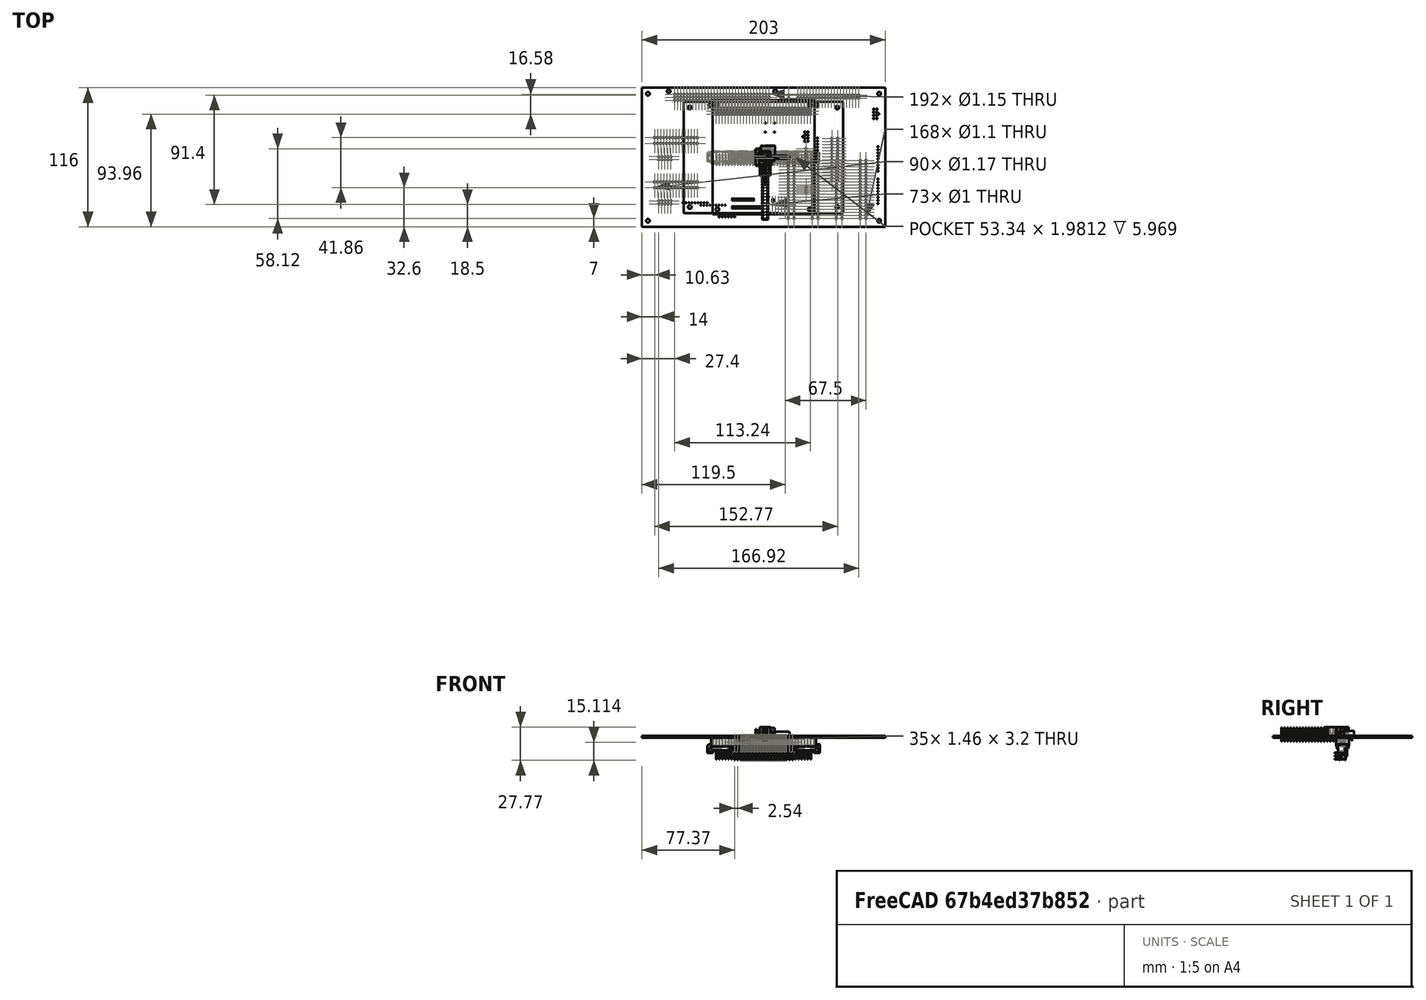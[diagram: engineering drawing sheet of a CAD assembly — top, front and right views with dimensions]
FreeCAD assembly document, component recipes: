
FREECAD ASSEMBLY — COMPONENT RECIPES ("GComputerCaseAssembly")

This assembly document has 216 components, labeled P0..P215 below (a component is one placed body or linked part). 0 of them carry a construction recipe — the FreeCAD feature program that regenerates the part from scratch, quoted from this document or its linked companion documents; the rest are supplied as boundary geometry only. No exploded tour is included for this assembly.
COMPONENT P0 — geometry summary ("FirstPartPeripherals"; no construction recipe available for this part):
  bounding box: 145.0 x 132.5 x 56.0 mm
  tessellated surface: 13,564 triangles
  volume: 118816 mm^3 (11% of its bounding box)
COMPONENT P1 — geometry summary ("SecondPartPeripherals"; no construction recipe available for this part):
  bounding box: 131.0 x 78.0 x 56.0 mm
  tessellated surface: 13,790 triangles
  volume: 66979 mm^3 (12% of its bounding box)
COMPONENT P2 — geometry summary ("FirstPartProcessor"; no construction recipe available for this part):
  bounding box: 147.0 x 120.6 x 56.0 mm
  tessellated surface: 38,998 triangles
  volume: 110022 mm^3 (11% of its bounding box)
COMPONENT P3 — geometry summary ("SecondPartProcessor"; no construction recipe available for this part):
  bounding box: 120.6 x 78.0 x 56.0 mm
  tessellated surface: 14,104 triangles
  volume: 61111 mm^3 (12% of its bounding box)
COMPONENT P4 — geometry summary ("C_0805_2012Metric001"; no construction recipe available for this part):
  bounding box: 2.0 x 1.2 x 1.2 mm
  tessellated surface: 188 triangles
  volume: 3 mm^3 (92% of its bounding box)
  symmetry: 4-fold rotationally symmetric about the x axis; 2-fold rotationally symmetric about the z axis; mirror-symmetric across its x mid-plane, y mid-plane
COMPONENT P5 — geometry summary ("C_0805_2012Metric002"; no construction recipe available for this part):
  bounding box: 2.0 x 1.2 x 1.2 mm
  tessellated surface: 188 triangles
  volume: 3 mm^3 (92% of its bounding box)
  symmetry: 4-fold rotationally symmetric about the x axis; 2-fold rotationally symmetric about the z axis; mirror-symmetric across its x mid-plane, y mid-plane
COMPONENT P6 — geometry summary ("C_0805_2012Metric003"; no construction recipe available for this part):
  bounding box: 2.0 x 1.2 x 1.2 mm
  tessellated surface: 188 triangles
  volume: 3 mm^3 (92% of its bounding box)
  symmetry: 4-fold rotationally symmetric about the x axis; 2-fold rotationally symmetric about the z axis; mirror-symmetric across its x mid-plane, y mid-plane
COMPONENT P7 — geometry summary ("C_0805_2012Metric004"; no construction recipe available for this part):
  bounding box: 2.0 x 1.2 x 1.2 mm
  tessellated surface: 188 triangles
  volume: 3 mm^3 (92% of its bounding box)
  symmetry: 4-fold rotationally symmetric about the x axis; 2-fold rotationally symmetric about the z axis; mirror-symmetric across its x mid-plane, y mid-plane
COMPONENT P8 — geometry summary ("C_0805_2012Metric005"; no construction recipe available for this part):
  bounding box: 2.0 x 1.2 x 1.2 mm
  tessellated surface: 188 triangles
  volume: 3 mm^3 (92% of its bounding box)
  symmetry: 4-fold rotationally symmetric about the x axis; 2-fold rotationally symmetric about the z axis; mirror-symmetric across its x mid-plane, y mid-plane
COMPONENT P9 — geometry summary ("C_0805_2012Metric006"; no construction recipe available for this part):
  bounding box: 2.0 x 1.2 x 1.2 mm
  tessellated surface: 188 triangles
  volume: 3 mm^3 (92% of its bounding box)
  symmetry: 4-fold rotationally symmetric about the x axis; 2-fold rotationally symmetric about the z axis; mirror-symmetric across its x mid-plane, y mid-plane
COMPONENT P10 — geometry summary ("C_0805_2012Metric007"; no construction recipe available for this part):
  bounding box: 2.0 x 1.2 x 1.2 mm
  tessellated surface: 188 triangles
  volume: 3 mm^3 (92% of its bounding box)
  symmetry: 4-fold rotationally symmetric about the x axis; 2-fold rotationally symmetric about the z axis; mirror-symmetric across its x mid-plane, y mid-plane
COMPONENT P11 — geometry summary ("C_0805_2012Metric008"; no construction recipe available for this part):
  bounding box: 2.0 x 1.2 x 1.2 mm
  tessellated surface: 188 triangles
  volume: 3 mm^3 (92% of its bounding box)
  symmetry: 4-fold rotationally symmetric about the x axis; 2-fold rotationally symmetric about the z axis; mirror-symmetric across its x mid-plane, y mid-plane
COMPONENT P12 — geometry summary ("C_0805_2012Metric009"; no construction recipe available for this part):
  bounding box: 2.0 x 1.2 x 1.2 mm
  tessellated surface: 188 triangles
  volume: 3 mm^3 (92% of its bounding box)
  symmetry: 4-fold rotationally symmetric about the x axis; 2-fold rotationally symmetric about the z axis; mirror-symmetric across its x mid-plane, y mid-plane
COMPONENT P13 — geometry summary ("C_0805_2012Metric010"; no construction recipe available for this part):
  bounding box: 2.0 x 1.2 x 1.2 mm
  tessellated surface: 188 triangles
  volume: 3 mm^3 (92% of its bounding box)
  symmetry: 4-fold rotationally symmetric about the x axis; 2-fold rotationally symmetric about the z axis; mirror-symmetric across its x mid-plane, y mid-plane
COMPONENT P14 — geometry summary ("C_0805_2012Metric011"; no construction recipe available for this part):
  bounding box: 2.0 x 1.2 x 1.2 mm
  tessellated surface: 188 triangles
  volume: 3 mm^3 (92% of its bounding box)
  symmetry: 4-fold rotationally symmetric about the x axis; 2-fold rotationally symmetric about the z axis; mirror-symmetric across its x mid-plane, y mid-plane
COMPONENT P15 — geometry summary ("C_0805_2012Metric012"; no construction recipe available for this part):
  bounding box: 2.0 x 1.2 x 1.2 mm
  tessellated surface: 188 triangles
  volume: 3 mm^3 (92% of its bounding box)
  symmetry: 4-fold rotationally symmetric about the x axis; 2-fold rotationally symmetric about the z axis; mirror-symmetric across its x mid-plane, y mid-plane
COMPONENT P16 — geometry summary ("C_0805_2012Metric013"; no construction recipe available for this part):
  bounding box: 2.0 x 1.2 x 1.2 mm
  tessellated surface: 188 triangles
  volume: 3 mm^3 (92% of its bounding box)
  symmetry: 4-fold rotationally symmetric about the x axis; 2-fold rotationally symmetric about the z axis; mirror-symmetric across its x mid-plane, y mid-plane
COMPONENT P17 — geometry summary ("C_0805_2012Metric014"; no construction recipe available for this part):
  bounding box: 2.0 x 1.2 x 1.2 mm
  tessellated surface: 188 triangles
  volume: 3 mm^3 (92% of its bounding box)
  symmetry: 4-fold rotationally symmetric about the x axis; 2-fold rotationally symmetric about the z axis; mirror-symmetric across its x mid-plane, y mid-plane
COMPONENT P18 — geometry summary ("C_0805_2012Metric015"; no construction recipe available for this part):
  bounding box: 2.0 x 1.2 x 1.2 mm
  tessellated surface: 188 triangles
  volume: 3 mm^3 (92% of its bounding box)
  symmetry: 4-fold rotationally symmetric about the x axis; 2-fold rotationally symmetric about the z axis; mirror-symmetric across its x mid-plane, y mid-plane
COMPONENT P19 — geometry summary ("C_0805_2012Metric016"; no construction recipe available for this part):
  bounding box: 2.0 x 1.2 x 1.2 mm
  tessellated surface: 188 triangles
  volume: 3 mm^3 (92% of its bounding box)
  symmetry: 4-fold rotationally symmetric about the x axis; 2-fold rotationally symmetric about the z axis; mirror-symmetric across its x mid-plane, y mid-plane
COMPONENT P20 — geometry summary ("C_0805_2012Metric017"; no construction recipe available for this part):
  bounding box: 2.0 x 1.2 x 1.2 mm
  tessellated surface: 188 triangles
  volume: 3 mm^3 (92% of its bounding box)
  symmetry: 4-fold rotationally symmetric about the x axis; 2-fold rotationally symmetric about the z axis; mirror-symmetric across its x mid-plane, y mid-plane
COMPONENT P21 — geometry summary ("C_0805_2012Metric018"; no construction recipe available for this part):
  bounding box: 2.0 x 1.2 x 1.2 mm
  tessellated surface: 188 triangles
  volume: 3 mm^3 (92% of its bounding box)
  symmetry: 4-fold rotationally symmetric about the x axis; 2-fold rotationally symmetric about the z axis; mirror-symmetric across its x mid-plane, y mid-plane
COMPONENT P22 — geometry summary ("C_0805_2012Metric019"; no construction recipe available for this part):
  bounding box: 2.0 x 1.2 x 1.2 mm
  tessellated surface: 188 triangles
  volume: 3 mm^3 (92% of its bounding box)
  symmetry: 4-fold rotationally symmetric about the x axis; 2-fold rotationally symmetric about the z axis; mirror-symmetric across its x mid-plane, y mid-plane
COMPONENT P23 — geometry summary ("C_0805_2012Metric020"; no construction recipe available for this part):
  bounding box: 2.0 x 1.2 x 1.2 mm
  tessellated surface: 188 triangles
  volume: 3 mm^3 (92% of its bounding box)
  symmetry: 4-fold rotationally symmetric about the x axis; 2-fold rotationally symmetric about the z axis; mirror-symmetric across its x mid-plane, y mid-plane
COMPONENT P24 — geometry summary ("C_0805_2012Metric021"; no construction recipe available for this part):
  bounding box: 2.0 x 1.2 x 1.2 mm
  tessellated surface: 188 triangles
  volume: 3 mm^3 (92% of its bounding box)
  symmetry: 4-fold rotationally symmetric about the x axis; 2-fold rotationally symmetric about the z axis; mirror-symmetric across its x mid-plane, y mid-plane
COMPONENT P25 — geometry summary ("C_0805_2012Metric022"; no construction recipe available for this part):
  bounding box: 2.0 x 1.2 x 1.2 mm
  tessellated surface: 188 triangles
  volume: 3 mm^3 (92% of its bounding box)
  symmetry: 4-fold rotationally symmetric about the x axis; 2-fold rotationally symmetric about the z axis; mirror-symmetric across its x mid-plane, y mid-plane
COMPONENT P26 — geometry summary ("C_0805_2012Metric023"; no construction recipe available for this part):
  bounding box: 2.0 x 1.2 x 1.2 mm
  tessellated surface: 188 triangles
  volume: 3 mm^3 (92% of its bounding box)
  symmetry: 4-fold rotationally symmetric about the x axis; 2-fold rotationally symmetric about the z axis; mirror-symmetric across its x mid-plane, y mid-plane
COMPONENT P27 — geometry summary ("C_0805_2012Metric024"; no construction recipe available for this part):
  bounding box: 2.0 x 1.2 x 1.2 mm
  tessellated surface: 188 triangles
  volume: 3 mm^3 (92% of its bounding box)
  symmetry: 4-fold rotationally symmetric about the x axis; 2-fold rotationally symmetric about the z axis; mirror-symmetric across its x mid-plane, y mid-plane
COMPONENT P28 — geometry summary ("C_0805_2012Metric025"; no construction recipe available for this part):
  bounding box: 2.0 x 1.2 x 1.2 mm
  tessellated surface: 188 triangles
  volume: 3 mm^3 (92% of its bounding box)
  symmetry: 4-fold rotationally symmetric about the x axis; 2-fold rotationally symmetric about the z axis; mirror-symmetric across its x mid-plane, y mid-plane
COMPONENT P29 — geometry summary ("C_0805_2012Metric026"; no construction recipe available for this part):
  bounding box: 2.0 x 1.2 x 1.2 mm
  tessellated surface: 188 triangles
  volume: 3 mm^3 (92% of its bounding box)
  symmetry: 4-fold rotationally symmetric about the x axis; 2-fold rotationally symmetric about the z axis; mirror-symmetric across its x mid-plane, y mid-plane
COMPONENT P30 — geometry summary ("C_0805_2012Metric027"; no construction recipe available for this part):
  bounding box: 2.0 x 1.2 x 1.2 mm
  tessellated surface: 188 triangles
  volume: 3 mm^3 (92% of its bounding box)
  symmetry: 4-fold rotationally symmetric about the x axis; 2-fold rotationally symmetric about the z axis; mirror-symmetric across its x mid-plane, y mid-plane
COMPONENT P31 — geometry summary ("C_0805_2012Metric028"; no construction recipe available for this part):
  bounding box: 2.0 x 1.2 x 1.2 mm
  tessellated surface: 188 triangles
  volume: 3 mm^3 (92% of its bounding box)
  symmetry: 4-fold rotationally symmetric about the x axis; 2-fold rotationally symmetric about the z axis; mirror-symmetric across its x mid-plane, y mid-plane
COMPONENT P32 — geometry summary ("C_0805_2012Metric029"; no construction recipe available for this part):
  bounding box: 2.0 x 1.2 x 1.2 mm
  tessellated surface: 188 triangles
  volume: 3 mm^3 (92% of its bounding box)
  symmetry: 4-fold rotationally symmetric about the x axis; 2-fold rotationally symmetric about the z axis; mirror-symmetric across its x mid-plane, y mid-plane
COMPONENT P33 — geometry summary ("C_0805_2012Metric030"; no construction recipe available for this part):
  bounding box: 2.0 x 1.2 x 1.2 mm
  tessellated surface: 188 triangles
  volume: 3 mm^3 (92% of its bounding box)
  symmetry: 4-fold rotationally symmetric about the x axis; 2-fold rotationally symmetric about the z axis; mirror-symmetric across its x mid-plane, y mid-plane
COMPONENT P34 — geometry summary ("C_0805_2012Metric031"; no construction recipe available for this part):
  bounding box: 2.0 x 1.2 x 1.2 mm
  tessellated surface: 188 triangles
  volume: 3 mm^3 (92% of its bounding box)
  symmetry: 4-fold rotationally symmetric about the x axis; 2-fold rotationally symmetric about the z axis; mirror-symmetric across its x mid-plane, y mid-plane
COMPONENT P35 — geometry summary ("C_0805_2012Metric032"; no construction recipe available for this part):
  bounding box: 2.0 x 1.2 x 1.2 mm
  tessellated surface: 188 triangles
  volume: 3 mm^3 (92% of its bounding box)
  symmetry: 4-fold rotationally symmetric about the x axis; 2-fold rotationally symmetric about the z axis; mirror-symmetric across its x mid-plane, y mid-plane
COMPONENT P36 — geometry summary ("C_0805_2012Metric033"; no construction recipe available for this part):
  bounding box: 2.0 x 1.2 x 1.2 mm
  tessellated surface: 188 triangles
  volume: 3 mm^3 (92% of its bounding box)
  symmetry: 4-fold rotationally symmetric about the x axis; 2-fold rotationally symmetric about the z axis; mirror-symmetric across its x mid-plane, y mid-plane
COMPONENT P37 — geometry summary ("C_0805_2012Metric034"; no construction recipe available for this part):
  bounding box: 2.0 x 1.2 x 1.2 mm
  tessellated surface: 188 triangles
  volume: 3 mm^3 (92% of its bounding box)
  symmetry: 4-fold rotationally symmetric about the x axis; 2-fold rotationally symmetric about the z axis; mirror-symmetric across its x mid-plane, y mid-plane
COMPONENT P38 — geometry summary ("C_0805_2012Metric035"; no construction recipe available for this part):
  bounding box: 2.0 x 1.2 x 1.2 mm
  tessellated surface: 188 triangles
  volume: 3 mm^3 (92% of its bounding box)
  symmetry: 4-fold rotationally symmetric about the x axis; 2-fold rotationally symmetric about the z axis; mirror-symmetric across its x mid-plane, y mid-plane
COMPONENT P39 — geometry summary ("C_0805_2012Metric036"; no construction recipe available for this part):
  bounding box: 2.0 x 1.2 x 1.2 mm
  tessellated surface: 188 triangles
  volume: 3 mm^3 (92% of its bounding box)
  symmetry: 4-fold rotationally symmetric about the x axis; 2-fold rotationally symmetric about the z axis; mirror-symmetric across its x mid-plane, y mid-plane
COMPONENT P40 — geometry summary ("C_0805_2012Metric037"; no construction recipe available for this part):
  bounding box: 2.0 x 1.2 x 1.2 mm
  tessellated surface: 188 triangles
  volume: 3 mm^3 (92% of its bounding box)
  symmetry: 4-fold rotationally symmetric about the x axis; 2-fold rotationally symmetric about the z axis; mirror-symmetric across its x mid-plane, y mid-plane
COMPONENT P41 — geometry summary ("C_0805_2012Metric038"; no construction recipe available for this part):
  bounding box: 2.0 x 1.2 x 1.2 mm
  tessellated surface: 188 triangles
  volume: 3 mm^3 (92% of its bounding box)
  symmetry: 4-fold rotationally symmetric about the x axis; 2-fold rotationally symmetric about the z axis; mirror-symmetric across its x mid-plane, y mid-plane
COMPONENT P42 — geometry summary ("C_0805_2012Metric039"; no construction recipe available for this part):
  bounding box: 2.0 x 1.2 x 1.2 mm
  tessellated surface: 188 triangles
  volume: 3 mm^3 (92% of its bounding box)
  symmetry: 4-fold rotationally symmetric about the x axis; 2-fold rotationally symmetric about the z axis; mirror-symmetric across its x mid-plane, y mid-plane
COMPONENT P43 — geometry summary ("C_0805_2012Metric040"; no construction recipe available for this part):
  bounding box: 2.0 x 1.2 x 1.2 mm
  tessellated surface: 188 triangles
  volume: 3 mm^3 (92% of its bounding box)
  symmetry: 4-fold rotationally symmetric about the x axis; 2-fold rotationally symmetric about the z axis; mirror-symmetric across its x mid-plane, y mid-plane
COMPONENT P44 — geometry summary ("C_0805_2012Metric041"; no construction recipe available for this part):
  bounding box: 2.0 x 1.2 x 1.2 mm
  tessellated surface: 188 triangles
  volume: 3 mm^3 (92% of its bounding box)
  symmetry: 4-fold rotationally symmetric about the x axis; 2-fold rotationally symmetric about the z axis; mirror-symmetric across its x mid-plane, y mid-plane
COMPONENT P45 — geometry summary ("C_0805_2012Metric042"; no construction recipe available for this part):
  bounding box: 2.0 x 1.2 x 1.2 mm
  tessellated surface: 188 triangles
  volume: 3 mm^3 (92% of its bounding box)
  symmetry: 4-fold rotationally symmetric about the x axis; 2-fold rotationally symmetric about the z axis; mirror-symmetric across its x mid-plane, y mid-plane
COMPONENT P46 — geometry summary ("LED_1206_3216Metric001"; no construction recipe available for this part):
  bounding box: 3.2 x 1.6 x 1.1 mm
  tessellated surface: 232 triangles
  volume: 4 mm^3 (74% of its bounding box)
  symmetry: 2-fold rotationally symmetric about the z axis; mirror-symmetric across its x mid-plane
COMPONENT P47 — geometry summary ("R_0805_2012Metric001"; no construction recipe available for this part):
  bounding box: 2.0 x 1.2 x 0.4 mm
  tessellated surface: 148 triangles
  volume: 1 mm^3 (93% of its bounding box)
  symmetry: mirror-symmetric across its x mid-plane, y mid-plane
COMPONENT P48 — geometry summary ("R_0805_2012Metric002"; no construction recipe available for this part):
  bounding box: 2.0 x 1.2 x 0.4 mm
  tessellated surface: 148 triangles
  volume: 1 mm^3 (93% of its bounding box)
  symmetry: mirror-symmetric across its x mid-plane, y mid-plane
COMPONENT P49 — geometry summary ("R_0805_2012Metric003"; no construction recipe available for this part):
  bounding box: 2.0 x 1.2 x 0.4 mm
  tessellated surface: 148 triangles
  volume: 1 mm^3 (93% of its bounding box)
  symmetry: mirror-symmetric across its x mid-plane, y mid-plane
COMPONENT P50 — geometry summary ("R_0805_2012Metric004"; no construction recipe available for this part):
  bounding box: 2.0 x 1.2 x 0.4 mm
  tessellated surface: 148 triangles
  volume: 1 mm^3 (93% of its bounding box)
  symmetry: mirror-symmetric across its x mid-plane, y mid-plane
COMPONENT P51 — geometry summary ("R_Array_SIP010"; no construction recipe available for this part):
  bounding box: 22.9 x 8.3 x 2.5 mm
  tessellated surface: 4,184 triangles
  volume: 274 mm^3 (58% of its bounding box)
  symmetry: 2-fold rotationally symmetric about the z axis; mirror-symmetric across its x mid-plane
COMPONENT P52 — geometry summary ("SOIC-14_3.9x8.7mm_P1.27mm001"; no construction recipe available for this part):
  bounding box: 8.7 x 6.0 x 1.7 mm
  tessellated surface: 1,424 triangles
  volume: 54 mm^3 (60% of its bounding box)
  symmetry: 2-fold rotationally symmetric about the z axis; mirror-symmetric across its x mid-plane, y mid-plane
COMPONENT P53 — geometry summary ("SOT-23-006"; no construction recipe available for this part):
  bounding box: 2.9 x 2.8 x 1.6 mm
  tessellated surface: 536 triangles
  volume: 7 mm^3 (52% of its bounding box)
  symmetry: mirror-symmetric across its x mid-plane
COMPONENT P54 — geometry summary ("SOIC-14_3.9x8.7mm_P1.27mm002"; no construction recipe available for this part):
  bounding box: 8.7 x 6.0 x 1.7 mm
  tessellated surface: 1,424 triangles
  volume: 54 mm^3 (60% of its bounding box)
  symmetry: 2-fold rotationally symmetric about the z axis; mirror-symmetric across its x mid-plane, y mid-plane
COMPONENT P55 — geometry summary ("SOIC-20W_7.5x12.8mm_P1.27mm001"; no construction recipe available for this part):
  bounding box: 12.8 x 10.3 x 2.7 mm
  tessellated surface: 1,976 triangles
  volume: 237 mm^3 (65% of its bounding box)
  symmetry: 2-fold rotationally symmetric about the z axis; mirror-symmetric across its x mid-plane, y mid-plane
COMPONENT P56 — geometry summary ("SOIC-16_3.9x9.9mm_P1.27mm001"; no construction recipe available for this part):
  bounding box: 9.9 x 6.0 x 1.7 mm
  tessellated surface: 1,608 triangles
  volume: 62 mm^3 (60% of its bounding box)
  symmetry: 2-fold rotationally symmetric about the z axis; mirror-symmetric across its y mid-plane
COMPONENT P57 — geometry summary ("SOT-23-007"; no construction recipe available for this part):
  bounding box: 2.9 x 2.8 x 1.6 mm
  tessellated surface: 536 triangles
  volume: 7 mm^3 (52% of its bounding box)
  symmetry: mirror-symmetric across its x mid-plane
COMPONENT P58 — geometry summary ("SOIC-16_3.9x9.9mm_P1.27mm002"; no construction recipe available for this part):
  bounding box: 9.9 x 6.0 x 1.7 mm
  tessellated surface: 1,608 triangles
  volume: 62 mm^3 (60% of its bounding box)
  symmetry: 2-fold rotationally symmetric about the z axis; mirror-symmetric across its y mid-plane
COMPONENT P59 — geometry summary ("SOT-23-008"; no construction recipe available for this part):
  bounding box: 2.9 x 2.8 x 1.6 mm
  tessellated surface: 536 triangles
  volume: 7 mm^3 (52% of its bounding box)
  symmetry: mirror-symmetric across its x mid-plane
COMPONENT P60 — geometry summary ("SOIC-16_3.9x9.9mm_P1.27mm003"; no construction recipe available for this part):
  bounding box: 9.9 x 6.0 x 1.7 mm
  tessellated surface: 1,608 triangles
  volume: 62 mm^3 (60% of its bounding box)
  symmetry: 2-fold rotationally symmetric about the z axis; mirror-symmetric across its y mid-plane
COMPONENT P61 — geometry summary ("SOIC-14_3.9x8.7mm_P1.27mm003"; no construction recipe available for this part):
  bounding box: 8.7 x 6.0 x 1.7 mm
  tessellated surface: 1,424 triangles
  volume: 54 mm^3 (60% of its bounding box)
  symmetry: 2-fold rotationally symmetric about the z axis; mirror-symmetric across its x mid-plane, y mid-plane
COMPONENT P62 — geometry summary ("SOIC-16_3.9x9.9mm_P1.27mm004"; no construction recipe available for this part):
  bounding box: 9.9 x 6.0 x 1.7 mm
  tessellated surface: 1,608 triangles
  volume: 62 mm^3 (60% of its bounding box)
  symmetry: 2-fold rotationally symmetric about the z axis; mirror-symmetric across its y mid-plane
COMPONENT P63 — geometry summary ("SOIC-14_3.9x8.7mm_P1.27mm004"; no construction recipe available for this part):
  bounding box: 8.7 x 6.0 x 1.7 mm
  tessellated surface: 1,424 triangles
  volume: 54 mm^3 (60% of its bounding box)
  symmetry: 2-fold rotationally symmetric about the z axis; mirror-symmetric across its x mid-plane, y mid-plane
COMPONENT P64 — geometry summary ("SOIC-16_3.9x9.9mm_P1.27mm005"; no construction recipe available for this part):
  bounding box: 9.9 x 6.0 x 1.7 mm
  tessellated surface: 1,608 triangles
  volume: 62 mm^3 (60% of its bounding box)
  symmetry: 2-fold rotationally symmetric about the z axis; mirror-symmetric across its y mid-plane
COMPONENT P65 — geometry summary ("SOIC-20W_7.5x12.8mm_P1.27mm002"; no construction recipe available for this part):
  bounding box: 12.8 x 10.3 x 2.7 mm
  tessellated surface: 1,976 triangles
  volume: 237 mm^3 (65% of its bounding box)
  symmetry: 2-fold rotationally symmetric about the z axis; mirror-symmetric across its x mid-plane, y mid-plane
COMPONENT P66 — geometry summary ("SOIC-16_3.9x9.9mm_P1.27mm006"; no construction recipe available for this part):
  bounding box: 9.9 x 6.0 x 1.7 mm
  tessellated surface: 1,608 triangles
  volume: 62 mm^3 (60% of its bounding box)
  symmetry: 2-fold rotationally symmetric about the z axis; mirror-symmetric across its y mid-plane
COMPONENT P67 — geometry summary ("SOIC-20W_7.5x12.8mm_P1.27mm003"; no construction recipe available for this part):
  bounding box: 12.8 x 10.3 x 2.7 mm
  tessellated surface: 1,976 triangles
  volume: 237 mm^3 (65% of its bounding box)
  symmetry: 2-fold rotationally symmetric about the z axis; mirror-symmetric across its x mid-plane, y mid-plane
COMPONENT P68 — geometry summary ("SOIC-20W_7.5x12.8mm_P1.27mm004"; no construction recipe available for this part):
  bounding box: 12.8 x 10.3 x 2.7 mm
  tessellated surface: 1,976 triangles
  volume: 237 mm^3 (65% of its bounding box)
  symmetry: 2-fold rotationally symmetric about the z axis; mirror-symmetric across its x mid-plane, y mid-plane
COMPONENT P69 — geometry summary ("SOIC-20W_7.5x12.8mm_P1.27mm005"; no construction recipe available for this part):
  bounding box: 12.8 x 10.3 x 2.7 mm
  tessellated surface: 1,976 triangles
  volume: 237 mm^3 (65% of its bounding box)
  symmetry: 2-fold rotationally symmetric about the z axis; mirror-symmetric across its x mid-plane, y mid-plane
COMPONENT P70 — geometry summary ("SOIC-20W_7.5x12.8mm_P1.27mm006"; no construction recipe available for this part):
  bounding box: 12.8 x 10.3 x 2.7 mm
  tessellated surface: 1,976 triangles
  volume: 237 mm^3 (65% of its bounding box)
  symmetry: 2-fold rotationally symmetric about the z axis; mirror-symmetric across its x mid-plane, y mid-plane
COMPONENT P71 — geometry summary ("SOIC-20W_7.5x12.8mm_P1.27mm007"; no construction recipe available for this part):
  bounding box: 12.8 x 10.3 x 2.7 mm
  tessellated surface: 1,976 triangles
  volume: 237 mm^3 (65% of its bounding box)
  symmetry: 2-fold rotationally symmetric about the z axis; mirror-symmetric across its x mid-plane, y mid-plane
COMPONENT P72 — geometry summary ("SOIC-20W_7.5x12.8mm_P1.27mm008"; no construction recipe available for this part):
  bounding box: 12.8 x 10.3 x 2.7 mm
  tessellated surface: 1,976 triangles
  volume: 237 mm^3 (65% of its bounding box)
  symmetry: 2-fold rotationally symmetric about the z axis; mirror-symmetric across its x mid-plane, y mid-plane
COMPONENT P73 — geometry summary ("SOT-23-009"; no construction recipe available for this part):
  bounding box: 2.9 x 2.8 x 1.6 mm
  tessellated surface: 536 triangles
  volume: 7 mm^3 (52% of its bounding box)
  symmetry: mirror-symmetric across its x mid-plane
COMPONENT P74 — geometry summary ("SOIC-20W_7.5x12.8mm_P1.27mm009"; no construction recipe available for this part):
  bounding box: 12.8 x 10.3 x 2.7 mm
  tessellated surface: 1,976 triangles
  volume: 237 mm^3 (65% of its bounding box)
  symmetry: 2-fold rotationally symmetric about the z axis; mirror-symmetric across its x mid-plane, y mid-plane
COMPONENT P75 — geometry summary ("SOIC-20W_7.5x12.8mm_P1.27mm010"; no construction recipe available for this part):
  bounding box: 12.8 x 10.3 x 2.7 mm
  tessellated surface: 1,976 triangles
  volume: 237 mm^3 (65% of its bounding box)
  symmetry: 2-fold rotationally symmetric about the z axis; mirror-symmetric across its x mid-plane, y mid-plane
COMPONENT P76 — geometry summary ("SOT-23-010"; no construction recipe available for this part):
  bounding box: 2.9 x 2.8 x 1.6 mm
  tessellated surface: 536 triangles
  volume: 7 mm^3 (52% of its bounding box)
  symmetry: mirror-symmetric across its x mid-plane
COMPONENT P77 — geometry summary ("SOIC-20W_7.5x12.8mm_P1.27mm011"; no construction recipe available for this part):
  bounding box: 12.8 x 10.3 x 2.7 mm
  tessellated surface: 1,976 triangles
  volume: 237 mm^3 (65% of its bounding box)
  symmetry: 2-fold rotationally symmetric about the z axis; mirror-symmetric across its x mid-plane, y mid-plane
COMPONENT P78 — geometry summary ("SOIC-20W_7.5x12.8mm_P1.27mm012"; no construction recipe available for this part):
  bounding box: 12.8 x 10.3 x 2.7 mm
  tessellated surface: 1,976 triangles
  volume: 237 mm^3 (65% of its bounding box)
  symmetry: 2-fold rotationally symmetric about the z axis; mirror-symmetric across its x mid-plane, y mid-plane
COMPONENT P79 — geometry summary ("SOIC-20W_7.5x12.8mm_P1.27mm013"; no construction recipe available for this part):
  bounding box: 12.8 x 10.3 x 2.7 mm
  tessellated surface: 1,976 triangles
  volume: 237 mm^3 (65% of its bounding box)
  symmetry: 2-fold rotationally symmetric about the z axis; mirror-symmetric across its x mid-plane, y mid-plane
COMPONENT P80 — geometry summary ("SOIC-20W_7.5x12.8mm_P1.27mm014"; no construction recipe available for this part):
  bounding box: 12.8 x 10.3 x 2.7 mm
  tessellated surface: 1,976 triangles
  volume: 237 mm^3 (65% of its bounding box)
  symmetry: 2-fold rotationally symmetric about the z axis; mirror-symmetric across its x mid-plane, y mid-plane
COMPONENT P81 — geometry summary ("SOIC-20W_7.5x12.8mm_P1.27mm015"; no construction recipe available for this part):
  bounding box: 12.8 x 10.3 x 2.7 mm
  tessellated surface: 1,976 triangles
  volume: 237 mm^3 (65% of its bounding box)
  symmetry: 2-fold rotationally symmetric about the z axis; mirror-symmetric across its x mid-plane, y mid-plane
COMPONENT P82 — geometry summary ("C_0805_2012Metric043"; no construction recipe available for this part):
  bounding box: 2.0 x 1.2 x 1.2 mm
  tessellated surface: 188 triangles
  volume: 3 mm^3 (92% of its bounding box)
  symmetry: 4-fold rotationally symmetric about the x axis; 2-fold rotationally symmetric about the z axis; mirror-symmetric across its x mid-plane, y mid-plane
COMPONENT P83 — geometry summary ("C_0805_2012Metric044"; no construction recipe available for this part):
  bounding box: 2.0 x 1.2 x 1.2 mm
  tessellated surface: 188 triangles
  volume: 3 mm^3 (92% of its bounding box)
  symmetry: 4-fold rotationally symmetric about the x axis; 2-fold rotationally symmetric about the z axis; mirror-symmetric across its x mid-plane, y mid-plane
COMPONENT P84 — geometry summary ("SOIC-16_3.9x9.9mm_P1.27mm007"; no construction recipe available for this part):
  bounding box: 9.9 x 6.0 x 1.7 mm
  tessellated surface: 1,608 triangles
  volume: 62 mm^3 (60% of its bounding box)
  symmetry: 2-fold rotationally symmetric about the z axis; mirror-symmetric across its y mid-plane
COMPONENT P85 — geometry summary ("SOT-23-011"; no construction recipe available for this part):
  bounding box: 2.9 x 2.8 x 1.6 mm
  tessellated surface: 536 triangles
  volume: 7 mm^3 (52% of its bounding box)
  symmetry: mirror-symmetric across its x mid-plane
COMPONENT P86 — geometry summary ("C_0805_2012Metric045"; no construction recipe available for this part):
  bounding box: 2.0 x 1.2 x 1.2 mm
  tessellated surface: 188 triangles
  volume: 3 mm^3 (92% of its bounding box)
  symmetry: 4-fold rotationally symmetric about the x axis; 2-fold rotationally symmetric about the z axis; mirror-symmetric across its x mid-plane, y mid-plane
COMPONENT P87 — geometry summary ("C_0805_2012Metric046"; no construction recipe available for this part):
  bounding box: 2.0 x 1.2 x 1.2 mm
  tessellated surface: 188 triangles
  volume: 3 mm^3 (92% of its bounding box)
  symmetry: 4-fold rotationally symmetric about the x axis; 2-fold rotationally symmetric about the z axis; mirror-symmetric across its x mid-plane, y mid-plane
COMPONENT P88 — geometry summary ("C_0805_2012Metric047"; no construction recipe available for this part):
  bounding box: 2.0 x 1.2 x 1.2 mm
  tessellated surface: 188 triangles
  volume: 3 mm^3 (92% of its bounding box)
  symmetry: 4-fold rotationally symmetric about the x axis; 2-fold rotationally symmetric about the z axis; mirror-symmetric across its x mid-plane, y mid-plane
COMPONENT P89 — geometry summary ("C_0805_2012Metric048"; no construction recipe available for this part):
  bounding box: 2.0 x 1.2 x 1.2 mm
  tessellated surface: 188 triangles
  volume: 3 mm^3 (92% of its bounding box)
  symmetry: 4-fold rotationally symmetric about the x axis; 2-fold rotationally symmetric about the z axis; mirror-symmetric across its x mid-plane, y mid-plane
COMPONENT P90 — geometry summary ("R_0805_2012Metric005"; no construction recipe available for this part):
  bounding box: 2.0 x 1.2 x 0.4 mm
  tessellated surface: 148 triangles
  volume: 1 mm^3 (93% of its bounding box)
  symmetry: mirror-symmetric across its x mid-plane, y mid-plane
COMPONENT P91 — geometry summary ("R_0805_2012Metric006"; no construction recipe available for this part):
  bounding box: 2.0 x 1.2 x 0.4 mm
  tessellated surface: 148 triangles
  volume: 1 mm^3 (93% of its bounding box)
  symmetry: mirror-symmetric across its x mid-plane, y mid-plane
COMPONENT P92 — geometry summary ("5530843-004"; no construction recipe available for this part):
  bounding box: 44.7 x 18.7 x 9.3 mm
  tessellated surface: 5,284 triangles
  volume: 4851 mm^3 (62% of its bounding box)
  symmetry: 2-fold rotationally symmetric about the z axis; mirror-symmetric across its x mid-plane, y mid-plane
COMPONENT P93 — geometry summary ("C_0805_2012Metric050"; no construction recipe available for this part):
  bounding box: 2.0 x 1.2 x 1.2 mm
  tessellated surface: 188 triangles
  volume: 3 mm^3 (92% of its bounding box)
  symmetry: 4-fold rotationally symmetric about the x axis; 2-fold rotationally symmetric about the z axis; mirror-symmetric across its x mid-plane, y mid-plane
COMPONENT P94 — geometry summary ("C_0805_2012Metric051"; no construction recipe available for this part):
  bounding box: 2.0 x 1.2 x 1.2 mm
  tessellated surface: 188 triangles
  volume: 3 mm^3 (92% of its bounding box)
  symmetry: 4-fold rotationally symmetric about the x axis; 2-fold rotationally symmetric about the z axis; mirror-symmetric across its x mid-plane, y mid-plane
COMPONENT P95 — geometry summary ("C_0805_2012Metric052"; no construction recipe available for this part):
  bounding box: 2.0 x 1.2 x 1.2 mm
  tessellated surface: 188 triangles
  volume: 3 mm^3 (92% of its bounding box)
  symmetry: 4-fold rotationally symmetric about the x axis; 2-fold rotationally symmetric about the z axis; mirror-symmetric across its x mid-plane, y mid-plane
COMPONENT P96 — geometry summary ("C_0805_2012Metric053"; no construction recipe available for this part):
  bounding box: 2.0 x 1.2 x 1.2 mm
  tessellated surface: 188 triangles
  volume: 3 mm^3 (92% of its bounding box)
  symmetry: 4-fold rotationally symmetric about the x axis; 2-fold rotationally symmetric about the z axis; mirror-symmetric across its x mid-plane, y mid-plane
COMPONENT P97 — geometry summary ("C_0805_2012Metric054"; no construction recipe available for this part):
  bounding box: 2.0 x 1.2 x 1.2 mm
  tessellated surface: 188 triangles
  volume: 3 mm^3 (92% of its bounding box)
  symmetry: 4-fold rotationally symmetric about the x axis; 2-fold rotationally symmetric about the z axis; mirror-symmetric across its x mid-plane, y mid-plane
COMPONENT P98 — geometry summary ("C_0805_2012Metric055"; no construction recipe available for this part):
  bounding box: 2.0 x 1.2 x 1.2 mm
  tessellated surface: 188 triangles
  volume: 3 mm^3 (92% of its bounding box)
  symmetry: 4-fold rotationally symmetric about the x axis; 2-fold rotationally symmetric about the z axis; mirror-symmetric across its x mid-plane, y mid-plane
COMPONENT P99 — geometry summary ("C_0805_2012Metric056"; no construction recipe available for this part):
  bounding box: 2.0 x 1.2 x 1.2 mm
  tessellated surface: 188 triangles
  volume: 3 mm^3 (92% of its bounding box)
  symmetry: 4-fold rotationally symmetric about the x axis; 2-fold rotationally symmetric about the z axis; mirror-symmetric across its x mid-plane, y mid-plane
COMPONENT P100 — geometry summary ("C_0805_2012Metric057"; no construction recipe available for this part):
  bounding box: 2.0 x 1.2 x 1.2 mm
  tessellated surface: 188 triangles
  volume: 3 mm^3 (92% of its bounding box)
  symmetry: 4-fold rotationally symmetric about the x axis; 2-fold rotationally symmetric about the z axis; mirror-symmetric across its x mid-plane, y mid-plane
COMPONENT P101 — geometry summary ("C_0805_2012Metric058"; no construction recipe available for this part):
  bounding box: 2.0 x 1.2 x 1.2 mm
  tessellated surface: 188 triangles
  volume: 3 mm^3 (92% of its bounding box)
  symmetry: 4-fold rotationally symmetric about the x axis; 2-fold rotationally symmetric about the z axis; mirror-symmetric across its x mid-plane, y mid-plane
COMPONENT P102 — geometry summary ("C_0805_2012Metric059"; no construction recipe available for this part):
  bounding box: 2.0 x 1.2 x 1.2 mm
  tessellated surface: 188 triangles
  volume: 3 mm^3 (92% of its bounding box)
  symmetry: 4-fold rotationally symmetric about the x axis; 2-fold rotationally symmetric about the z axis; mirror-symmetric across its x mid-plane, y mid-plane
COMPONENT P103 — geometry summary ("C_0805_2012Metric060"; no construction recipe available for this part):
  bounding box: 2.0 x 1.2 x 1.2 mm
  tessellated surface: 188 triangles
  volume: 3 mm^3 (92% of its bounding box)
  symmetry: 4-fold rotationally symmetric about the x axis; 2-fold rotationally symmetric about the z axis; mirror-symmetric across its x mid-plane, y mid-plane
COMPONENT P104 — geometry summary ("C_0805_2012Metric061"; no construction recipe available for this part):
  bounding box: 2.0 x 1.2 x 1.2 mm
  tessellated surface: 188 triangles
  volume: 3 mm^3 (92% of its bounding box)
  symmetry: 4-fold rotationally symmetric about the x axis; 2-fold rotationally symmetric about the z axis; mirror-symmetric across its x mid-plane, y mid-plane
COMPONENT P105 — geometry summary ("C_0805_2012Metric062"; no construction recipe available for this part):
  bounding box: 2.0 x 1.2 x 1.2 mm
  tessellated surface: 188 triangles
  volume: 3 mm^3 (92% of its bounding box)
  symmetry: 4-fold rotationally symmetric about the x axis; 2-fold rotationally symmetric about the z axis; mirror-symmetric across its x mid-plane, y mid-plane
COMPONENT P106 — geometry summary ("C_0805_2012Metric063"; no construction recipe available for this part):
  bounding box: 2.0 x 1.2 x 1.2 mm
  tessellated surface: 188 triangles
  volume: 3 mm^3 (92% of its bounding box)
  symmetry: 4-fold rotationally symmetric about the x axis; 2-fold rotationally symmetric about the z axis; mirror-symmetric across its x mid-plane, y mid-plane
COMPONENT P107 — geometry summary ("C_0805_2012Metric064"; no construction recipe available for this part):
  bounding box: 2.0 x 1.2 x 1.2 mm
  tessellated surface: 188 triangles
  volume: 3 mm^3 (92% of its bounding box)
  symmetry: 4-fold rotationally symmetric about the x axis; 2-fold rotationally symmetric about the z axis; mirror-symmetric across its x mid-plane, y mid-plane
COMPONENT P108 — geometry summary ("C_0805_2012Metric065"; no construction recipe available for this part):
  bounding box: 2.0 x 1.2 x 1.2 mm
  tessellated surface: 188 triangles
  volume: 3 mm^3 (92% of its bounding box)
  symmetry: 4-fold rotationally symmetric about the x axis; 2-fold rotationally symmetric about the z axis; mirror-symmetric across its x mid-plane, y mid-plane
COMPONENT P109 — geometry summary ("C_0805_2012Metric066"; no construction recipe available for this part):
  bounding box: 2.0 x 1.2 x 1.2 mm
  tessellated surface: 188 triangles
  volume: 3 mm^3 (92% of its bounding box)
  symmetry: 4-fold rotationally symmetric about the x axis; 2-fold rotationally symmetric about the z axis; mirror-symmetric across its x mid-plane, y mid-plane
COMPONENT P110 — geometry summary ("C_0805_2012Metric067"; no construction recipe available for this part):
  bounding box: 2.0 x 1.2 x 1.2 mm
  tessellated surface: 188 triangles
  volume: 3 mm^3 (92% of its bounding box)
  symmetry: 4-fold rotationally symmetric about the x axis; 2-fold rotationally symmetric about the z axis; mirror-symmetric across its x mid-plane, y mid-plane
COMPONENT P111 — geometry summary ("C_0805_2012Metric068"; no construction recipe available for this part):
  bounding box: 2.0 x 1.2 x 1.2 mm
  tessellated surface: 188 triangles
  volume: 3 mm^3 (92% of its bounding box)
  symmetry: 4-fold rotationally symmetric about the x axis; 2-fold rotationally symmetric about the z axis; mirror-symmetric across its x mid-plane, y mid-plane
COMPONENT P112 — geometry summary ("C_0805_2012Metric069"; no construction recipe available for this part):
  bounding box: 2.0 x 1.2 x 1.2 mm
  tessellated surface: 188 triangles
  volume: 3 mm^3 (92% of its bounding box)
  symmetry: 4-fold rotationally symmetric about the x axis; 2-fold rotationally symmetric about the z axis; mirror-symmetric across its x mid-plane, y mid-plane
COMPONENT P113 — geometry summary ("C_0805_2012Metric070"; no construction recipe available for this part):
  bounding box: 2.0 x 1.2 x 1.2 mm
  tessellated surface: 188 triangles
  volume: 3 mm^3 (92% of its bounding box)
  symmetry: 4-fold rotationally symmetric about the x axis; 2-fold rotationally symmetric about the z axis; mirror-symmetric across its x mid-plane, y mid-plane
COMPONENT P114 — geometry summary ("C_0805_2012Metric071"; no construction recipe available for this part):
  bounding box: 2.0 x 1.2 x 1.2 mm
  tessellated surface: 188 triangles
  volume: 3 mm^3 (92% of its bounding box)
  symmetry: 4-fold rotationally symmetric about the x axis; 2-fold rotationally symmetric about the z axis; mirror-symmetric across its x mid-plane, y mid-plane
COMPONENT P115 — geometry summary ("C_0805_2012Metric072"; no construction recipe available for this part):
  bounding box: 2.0 x 1.2 x 1.2 mm
  tessellated surface: 188 triangles
  volume: 3 mm^3 (92% of its bounding box)
  symmetry: 4-fold rotationally symmetric about the x axis; 2-fold rotationally symmetric about the z axis; mirror-symmetric across its x mid-plane, y mid-plane
COMPONENT P116 — geometry summary ("C_0805_2012Metric073"; no construction recipe available for this part):
  bounding box: 2.0 x 1.2 x 1.2 mm
  tessellated surface: 188 triangles
  volume: 3 mm^3 (92% of its bounding box)
  symmetry: 4-fold rotationally symmetric about the x axis; 2-fold rotationally symmetric about the z axis; mirror-symmetric across its x mid-plane, y mid-plane
COMPONENT P117 — geometry summary ("C_0805_2012Metric074"; no construction recipe available for this part):
  bounding box: 2.0 x 1.2 x 1.2 mm
  tessellated surface: 188 triangles
  volume: 3 mm^3 (92% of its bounding box)
  symmetry: 4-fold rotationally symmetric about the x axis; 2-fold rotationally symmetric about the z axis; mirror-symmetric across its x mid-plane, y mid-plane
COMPONENT P118 — geometry summary ("C_0805_2012Metric075"; no construction recipe available for this part):
  bounding box: 2.0 x 1.2 x 1.2 mm
  tessellated surface: 188 triangles
  volume: 3 mm^3 (92% of its bounding box)
  symmetry: 4-fold rotationally symmetric about the x axis; 2-fold rotationally symmetric about the z axis; mirror-symmetric across its x mid-plane, y mid-plane
COMPONENT P119 — geometry summary ("C_0805_2012Metric076"; no construction recipe available for this part):
  bounding box: 2.0 x 1.2 x 1.2 mm
  tessellated surface: 188 triangles
  volume: 3 mm^3 (92% of its bounding box)
  symmetry: 4-fold rotationally symmetric about the x axis; 2-fold rotationally symmetric about the z axis; mirror-symmetric across its x mid-plane, y mid-plane
COMPONENT P120 — geometry summary ("C_0805_2012Metric077"; no construction recipe available for this part):
  bounding box: 2.0 x 1.2 x 1.2 mm
  tessellated surface: 188 triangles
  volume: 3 mm^3 (92% of its bounding box)
  symmetry: 4-fold rotationally symmetric about the x axis; 2-fold rotationally symmetric about the z axis; mirror-symmetric across its x mid-plane, y mid-plane
COMPONENT P121 — geometry summary ("C_0805_2012Metric078"; no construction recipe available for this part):
  bounding box: 2.0 x 1.2 x 1.2 mm
  tessellated surface: 188 triangles
  volume: 3 mm^3 (92% of its bounding box)
  symmetry: 4-fold rotationally symmetric about the x axis; 2-fold rotationally symmetric about the z axis; mirror-symmetric across its x mid-plane, y mid-plane
COMPONENT P122 — geometry summary ("C_0805_2012Metric079"; no construction recipe available for this part):
  bounding box: 2.0 x 1.2 x 1.2 mm
  tessellated surface: 188 triangles
  volume: 3 mm^3 (92% of its bounding box)
  symmetry: 4-fold rotationally symmetric about the x axis; 2-fold rotationally symmetric about the z axis; mirror-symmetric across its x mid-plane, y mid-plane
COMPONENT P123 — geometry summary ("C_0805_2012Metric080"; no construction recipe available for this part):
  bounding box: 2.0 x 1.2 x 1.2 mm
  tessellated surface: 188 triangles
  volume: 3 mm^3 (92% of its bounding box)
  symmetry: 4-fold rotationally symmetric about the x axis; 2-fold rotationally symmetric about the z axis; mirror-symmetric across its x mid-plane, y mid-plane
COMPONENT P124 — geometry summary ("C_0805_2012Metric081"; no construction recipe available for this part):
  bounding box: 2.0 x 1.2 x 1.2 mm
  tessellated surface: 188 triangles
  volume: 3 mm^3 (92% of its bounding box)
  symmetry: 4-fold rotationally symmetric about the x axis; 2-fold rotationally symmetric about the z axis; mirror-symmetric across its x mid-plane, y mid-plane
COMPONENT P125 — geometry summary ("C_0805_2012Metric082"; no construction recipe available for this part):
  bounding box: 2.0 x 1.2 x 1.2 mm
  tessellated surface: 188 triangles
  volume: 3 mm^3 (92% of its bounding box)
  symmetry: 4-fold rotationally symmetric about the x axis; 2-fold rotationally symmetric about the z axis; mirror-symmetric across its x mid-plane, y mid-plane
COMPONENT P126 — geometry summary ("C_0805_2012Metric083"; no construction recipe available for this part):
  bounding box: 2.0 x 1.2 x 1.2 mm
  tessellated surface: 188 triangles
  volume: 3 mm^3 (92% of its bounding box)
  symmetry: 4-fold rotationally symmetric about the x axis; 2-fold rotationally symmetric about the z axis; mirror-symmetric across its x mid-plane, y mid-plane
COMPONENT P127 — geometry summary ("C_0805_2012Metric084"; no construction recipe available for this part):
  bounding box: 2.0 x 1.2 x 1.2 mm
  tessellated surface: 188 triangles
  volume: 3 mm^3 (92% of its bounding box)
  symmetry: 4-fold rotationally symmetric about the x axis; 2-fold rotationally symmetric about the z axis; mirror-symmetric across its x mid-plane, y mid-plane
COMPONENT P128 — geometry summary ("C_0805_2012Metric085"; no construction recipe available for this part):
  bounding box: 2.0 x 1.2 x 1.2 mm
  tessellated surface: 188 triangles
  volume: 3 mm^3 (92% of its bounding box)
  symmetry: 4-fold rotationally symmetric about the x axis; 2-fold rotationally symmetric about the z axis; mirror-symmetric across its x mid-plane, y mid-plane
COMPONENT P129 — geometry summary ("C_0805_2012Metric086"; no construction recipe available for this part):
  bounding box: 2.0 x 1.2 x 1.2 mm
  tessellated surface: 188 triangles
  volume: 3 mm^3 (92% of its bounding box)
  symmetry: 4-fold rotationally symmetric about the x axis; 2-fold rotationally symmetric about the z axis; mirror-symmetric across its x mid-plane, y mid-plane
COMPONENT P130 — geometry summary ("R_0805_2012Metric008"; no construction recipe available for this part):
  bounding box: 2.0 x 1.2 x 0.4 mm
  tessellated surface: 148 triangles
  volume: 1 mm^3 (93% of its bounding box)
  symmetry: mirror-symmetric across its x mid-plane, y mid-plane
COMPONENT P131 — geometry summary ("R_0805_2012Metric009"; no construction recipe available for this part):
  bounding box: 2.0 x 1.2 x 0.4 mm
  tessellated surface: 148 triangles
  volume: 1 mm^3 (93% of its bounding box)
  symmetry: mirror-symmetric across its x mid-plane, y mid-plane
COMPONENT P132 — geometry summary ("R_0805_2012Metric010"; no construction recipe available for this part):
  bounding box: 2.0 x 1.2 x 0.4 mm
  tessellated surface: 148 triangles
  volume: 1 mm^3 (93% of its bounding box)
  symmetry: mirror-symmetric across its x mid-plane, y mid-plane
COMPONENT P133 — geometry summary ("R_0805_2012Metric011"; no construction recipe available for this part):
  bounding box: 2.0 x 1.2 x 0.4 mm
  tessellated surface: 148 triangles
  volume: 1 mm^3 (93% of its bounding box)
  symmetry: mirror-symmetric across its x mid-plane, y mid-plane
COMPONENT P134 — geometry summary ("R_Array_SIP012"; no construction recipe available for this part):
  bounding box: 22.9 x 8.3 x 2.5 mm
  tessellated surface: 4,184 triangles
  volume: 274 mm^3 (58% of its bounding box)
  symmetry: 2-fold rotationally symmetric about the z axis; mirror-symmetric across its x mid-plane
COMPONENT P135 — geometry summary ("R_Array_SIP013"; no construction recipe available for this part):
  bounding box: 22.9 x 8.3 x 2.5 mm
  tessellated surface: 4,184 triangles
  volume: 274 mm^3 (58% of its bounding box)
  symmetry: 2-fold rotationally symmetric about the z axis; mirror-symmetric across its x mid-plane
COMPONENT P136 — geometry summary ("SOT-23-013"; no construction recipe available for this part):
  bounding box: 2.9 x 2.8 x 1.6 mm
  tessellated surface: 536 triangles
  volume: 7 mm^3 (52% of its bounding box)
  symmetry: mirror-symmetric across its y mid-plane
COMPONENT P137 — geometry summary ("SOIC-20W_7.5x12.8mm_P1.27mm017"; no construction recipe available for this part):
  bounding box: 12.8 x 10.3 x 2.7 mm
  tessellated surface: 1,976 triangles
  volume: 237 mm^3 (65% of its bounding box)
  symmetry: 2-fold rotationally symmetric about the z axis; mirror-symmetric across its x mid-plane, y mid-plane
COMPONENT P138 — geometry summary ("SOIC-20W_7.5x12.8mm_P1.27mm018"; no construction recipe available for this part):
  bounding box: 12.8 x 10.3 x 2.7 mm
  tessellated surface: 1,976 triangles
  volume: 237 mm^3 (65% of its bounding box)
  symmetry: 2-fold rotationally symmetric about the z axis; mirror-symmetric across its x mid-plane, y mid-plane
COMPONENT P139 — geometry summary ("SOT-23-014"; no construction recipe available for this part):
  bounding box: 2.9 x 2.8 x 1.6 mm
  tessellated surface: 536 triangles
  volume: 7 mm^3 (52% of its bounding box)
  symmetry: mirror-symmetric across its y mid-plane
COMPONENT P140 — geometry summary ("SOIC-20W_7.5x12.8mm_P1.27mm019"; no construction recipe available for this part):
  bounding box: 12.8 x 10.3 x 2.7 mm
  tessellated surface: 1,976 triangles
  volume: 237 mm^3 (65% of its bounding box)
  symmetry: 2-fold rotationally symmetric about the z axis; mirror-symmetric across its x mid-plane, y mid-plane
COMPONENT P141 — geometry summary ("SOT-23-015"; no construction recipe available for this part):
  bounding box: 2.9 x 2.8 x 1.6 mm
  tessellated surface: 536 triangles
  volume: 7 mm^3 (52% of its bounding box)
  symmetry: mirror-symmetric across its y mid-plane
COMPONENT P142 — geometry summary ("SOT-23-016"; no construction recipe available for this part):
  bounding box: 2.9 x 2.8 x 1.6 mm
  tessellated surface: 536 triangles
  volume: 7 mm^3 (52% of its bounding box)
  symmetry: mirror-symmetric across its y mid-plane
COMPONENT P143 — geometry summary ("SOIC-20W_7.5x12.8mm_P1.27mm020"; no construction recipe available for this part):
  bounding box: 12.8 x 10.3 x 2.7 mm
  tessellated surface: 1,976 triangles
  volume: 237 mm^3 (65% of its bounding box)
  symmetry: 2-fold rotationally symmetric about the z axis; mirror-symmetric across its x mid-plane, y mid-plane
COMPONENT P144 — geometry summary ("TSSOP-56_6.1x14mm_P0.5mm001"; no construction recipe available for this part):
  bounding box: 14.0 x 8.1 x 1.1 mm
  tessellated surface: 5,280 triangles
  volume: 81 mm^3 (68% of its bounding box)
  symmetry: 2-fold rotationally symmetric about the z axis; mirror-symmetric across its y mid-plane
COMPONENT P145 — geometry summary ("TSSOP-56_6.1x14mm_P0.5mm002"; no construction recipe available for this part):
  bounding box: 14.0 x 8.1 x 1.1 mm
  tessellated surface: 5,280 triangles
  volume: 81 mm^3 (68% of its bounding box)
  symmetry: 2-fold rotationally symmetric about the z axis; mirror-symmetric across its y mid-plane
COMPONENT P146 — geometry summary ("C_0805_2012Metric087"; no construction recipe available for this part):
  bounding box: 2.0 x 1.2 x 1.2 mm
  tessellated surface: 188 triangles
  volume: 3 mm^3 (92% of its bounding box)
  symmetry: 4-fold rotationally symmetric about the x axis; 2-fold rotationally symmetric about the z axis; mirror-symmetric across its x mid-plane, y mid-plane
COMPONENT P147 — geometry summary ("C_0805_2012Metric088"; no construction recipe available for this part):
  bounding box: 2.0 x 1.2 x 1.2 mm
  tessellated surface: 188 triangles
  volume: 3 mm^3 (92% of its bounding box)
  symmetry: 4-fold rotationally symmetric about the x axis; 2-fold rotationally symmetric about the z axis; mirror-symmetric across its x mid-plane, y mid-plane
COMPONENT P148 — geometry summary ("C_0805_2012Metric089"; no construction recipe available for this part):
  bounding box: 2.0 x 1.2 x 1.2 mm
  tessellated surface: 188 triangles
  volume: 3 mm^3 (92% of its bounding box)
  symmetry: 4-fold rotationally symmetric about the x axis; 2-fold rotationally symmetric about the z axis; mirror-symmetric across its x mid-plane, y mid-plane
COMPONENT P149 — geometry summary ("C_0805_2012Metric090"; no construction recipe available for this part):
  bounding box: 2.0 x 1.2 x 1.2 mm
  tessellated surface: 188 triangles
  volume: 3 mm^3 (92% of its bounding box)
  symmetry: 4-fold rotationally symmetric about the x axis; 2-fold rotationally symmetric about the z axis; mirror-symmetric across its x mid-plane, y mid-plane
COMPONENT P150 — geometry summary ("C_0805_2012Metric091"; no construction recipe available for this part):
  bounding box: 2.0 x 1.2 x 1.2 mm
  tessellated surface: 188 triangles
  volume: 3 mm^3 (92% of its bounding box)
  symmetry: 4-fold rotationally symmetric about the x axis; 2-fold rotationally symmetric about the z axis; mirror-symmetric across its x mid-plane, y mid-plane
COMPONENT P151 — geometry summary ("C_0805_2012Metric092"; no construction recipe available for this part):
  bounding box: 2.0 x 1.2 x 1.2 mm
  tessellated surface: 188 triangles
  volume: 3 mm^3 (92% of its bounding box)
  symmetry: 4-fold rotationally symmetric about the x axis; 2-fold rotationally symmetric about the z axis; mirror-symmetric across its x mid-plane, y mid-plane
COMPONENT P152 — geometry summary ("C_0805_2012Metric093"; no construction recipe available for this part):
  bounding box: 2.0 x 1.2 x 1.2 mm
  tessellated surface: 188 triangles
  volume: 3 mm^3 (92% of its bounding box)
  symmetry: 4-fold rotationally symmetric about the x axis; 2-fold rotationally symmetric about the z axis; mirror-symmetric across its x mid-plane, y mid-plane
COMPONENT P153 — geometry summary ("C_0805_2012Metric094"; no construction recipe available for this part):
  bounding box: 2.0 x 1.2 x 1.2 mm
  tessellated surface: 188 triangles
  volume: 3 mm^3 (92% of its bounding box)
  symmetry: 4-fold rotationally symmetric about the x axis; 2-fold rotationally symmetric about the z axis; mirror-symmetric across its x mid-plane, y mid-plane
COMPONENT P154 — geometry summary ("C_0805_2012Metric095"; no construction recipe available for this part):
  bounding box: 2.0 x 1.2 x 1.2 mm
  tessellated surface: 188 triangles
  volume: 3 mm^3 (92% of its bounding box)
  symmetry: 4-fold rotationally symmetric about the x axis; 2-fold rotationally symmetric about the z axis; mirror-symmetric across its x mid-plane, y mid-plane
COMPONENT P155 — geometry summary ("C_0805_2012Metric096"; no construction recipe available for this part):
  bounding box: 2.0 x 1.2 x 1.2 mm
  tessellated surface: 188 triangles
  volume: 3 mm^3 (92% of its bounding box)
  symmetry: 4-fold rotationally symmetric about the x axis; 2-fold rotationally symmetric about the z axis; mirror-symmetric across its x mid-plane, y mid-plane
COMPONENT P156 — geometry summary ("C_0805_2012Metric097"; no construction recipe available for this part):
  bounding box: 2.0 x 1.2 x 1.2 mm
  tessellated surface: 188 triangles
  volume: 3 mm^3 (92% of its bounding box)
  symmetry: 4-fold rotationally symmetric about the x axis; 2-fold rotationally symmetric about the z axis; mirror-symmetric across its x mid-plane, y mid-plane
COMPONENT P157 — geometry summary ("C_0805_2012Metric098"; no construction recipe available for this part):
  bounding box: 2.0 x 1.2 x 1.2 mm
  tessellated surface: 188 triangles
  volume: 3 mm^3 (92% of its bounding box)
  symmetry: 4-fold rotationally symmetric about the x axis; 2-fold rotationally symmetric about the z axis; mirror-symmetric across its x mid-plane, y mid-plane
COMPONENT P158 — geometry summary ("C_0805_2012Metric099"; no construction recipe available for this part):
  bounding box: 2.0 x 1.2 x 1.2 mm
  tessellated surface: 188 triangles
  volume: 3 mm^3 (92% of its bounding box)
  symmetry: 4-fold rotationally symmetric about the x axis; 2-fold rotationally symmetric about the z axis; mirror-symmetric across its x mid-plane, y mid-plane
COMPONENT P159 — geometry summary ("C_0805_2012Metric100"; no construction recipe available for this part):
  bounding box: 2.0 x 1.2 x 1.2 mm
  tessellated surface: 188 triangles
  volume: 3 mm^3 (92% of its bounding box)
  symmetry: 4-fold rotationally symmetric about the x axis; 2-fold rotationally symmetric about the z axis; mirror-symmetric across its x mid-plane, y mid-plane
COMPONENT P160 — geometry summary ("TE_5-5530843-005"; no construction recipe available for this part):
  bounding box: 57.4 x 18.7 x 9.3 mm
  tessellated surface: 6,724 triangles
  volume: 6234 mm^3 (62% of its bounding box)
  symmetry: 2-fold rotationally symmetric about the z axis; mirror-symmetric across its y mid-plane
COMPONENT P161 — geometry summary ("TE_5-5530843-006"; no construction recipe available for this part):
  bounding box: 57.4 x 18.7 x 9.3 mm
  tessellated surface: 6,724 triangles
  volume: 6234 mm^3 (62% of its bounding box)
  symmetry: 2-fold rotationally symmetric about the z axis; mirror-symmetric across its y mid-plane
COMPONENT P162 — geometry summary ("TE_5-5530843-007"; no construction recipe available for this part):
  bounding box: 57.4 x 18.7 x 9.3 mm
  tessellated surface: 6,724 triangles
  volume: 6234 mm^3 (62% of its bounding box)
  symmetry: 2-fold rotationally symmetric about the z axis; mirror-symmetric across its y mid-plane
COMPONENT P163 — geometry summary ("R_0805_2012Metric012"; no construction recipe available for this part):
  bounding box: 2.0 x 1.2 x 0.4 mm
  tessellated surface: 148 triangles
  volume: 1 mm^3 (93% of its bounding box)
  symmetry: mirror-symmetric across its x mid-plane, y mid-plane
COMPONENT P164 — geometry summary ("SOIC-16_3.9x9.9mm_P1.27mm009"; no construction recipe available for this part):
  bounding box: 9.9 x 6.0 x 1.7 mm
  tessellated surface: 1,608 triangles
  volume: 62 mm^3 (60% of its bounding box)
  symmetry: 2-fold rotationally symmetric about the z axis; mirror-symmetric across its x mid-plane
COMPONENT P165 — geometry summary ("SOIC-16_3.9x9.9mm_P1.27mm010"; no construction recipe available for this part):
  bounding box: 9.9 x 6.0 x 1.7 mm
  tessellated surface: 1,608 triangles
  volume: 62 mm^3 (60% of its bounding box)
  symmetry: 2-fold rotationally symmetric about the z axis; mirror-symmetric across its x mid-plane
COMPONENT P166 — geometry summary ("SOIC-16_3.9x9.9mm_P1.27mm011"; no construction recipe available for this part):
  bounding box: 9.9 x 6.0 x 1.7 mm
  tessellated surface: 1,608 triangles
  volume: 62 mm^3 (60% of its bounding box)
  symmetry: 2-fold rotationally symmetric about the z axis; mirror-symmetric across its x mid-plane
COMPONENT P167 — geometry summary ("SOIC-16_3.9x9.9mm_P1.27mm012"; no construction recipe available for this part):
  bounding box: 9.9 x 6.0 x 1.7 mm
  tessellated surface: 1,608 triangles
  volume: 62 mm^3 (60% of its bounding box)
  symmetry: 2-fold rotationally symmetric about the z axis; mirror-symmetric across its x mid-plane
COMPONENT P168 — geometry summary ("SOIC-16_3.9x9.9mm_P1.27mm013"; no construction recipe available for this part):
  bounding box: 9.9 x 6.0 x 1.7 mm
  tessellated surface: 1,608 triangles
  volume: 62 mm^3 (60% of its bounding box)
  symmetry: 2-fold rotationally symmetric about the z axis; mirror-symmetric across its x mid-plane
COMPONENT P169 — geometry summary ("SOIC-16_3.9x9.9mm_P1.27mm014"; no construction recipe available for this part):
  bounding box: 9.9 x 6.0 x 1.7 mm
  tessellated surface: 1,608 triangles
  volume: 62 mm^3 (60% of its bounding box)
  symmetry: 2-fold rotationally symmetric about the z axis; mirror-symmetric across its x mid-plane
COMPONENT P170 — geometry summary ("SOT-23-017"; no construction recipe available for this part):
  bounding box: 2.9 x 2.8 x 1.6 mm
  tessellated surface: 536 triangles
  volume: 7 mm^3 (52% of its bounding box)
  symmetry: mirror-symmetric across its y mid-plane
COMPONENT P171 — geometry summary ("SOIC-14_3.9x8.7mm_P1.27mm006"; no construction recipe available for this part):
  bounding box: 8.7 x 6.0 x 1.8 mm
  tessellated surface: 1,424 triangles
  volume: 54 mm^3 (60% of its bounding box)
  symmetry: 2-fold rotationally symmetric about the z axis; mirror-symmetric across its x mid-plane, y mid-plane
COMPONENT P172 — geometry summary ("SOIC-16_3.9x9.9mm_P1.27mm015"; no construction recipe available for this part):
  bounding box: 9.9 x 6.0 x 1.7 mm
  tessellated surface: 1,608 triangles
  volume: 62 mm^3 (60% of its bounding box)
  symmetry: 2-fold rotationally symmetric about the z axis; mirror-symmetric across its x mid-plane
COMPONENT P173 — geometry summary ("SOIC-16_3.9x9.9mm_P1.27mm016"; no construction recipe available for this part):
  bounding box: 9.9 x 6.0 x 1.7 mm
  tessellated surface: 1,608 triangles
  volume: 62 mm^3 (60% of its bounding box)
  symmetry: 2-fold rotationally symmetric about the z axis; mirror-symmetric across its x mid-plane
COMPONENT P174 — geometry summary ("SOT-23-018"; no construction recipe available for this part):
  bounding box: 2.9 x 2.8 x 1.6 mm
  tessellated surface: 536 triangles
  volume: 7 mm^3 (52% of its bounding box)
  symmetry: mirror-symmetric across its y mid-plane
COMPONENT P175 — geometry summary ("SOIC-16_3.9x9.9mm_P1.27mm017"; no construction recipe available for this part):
  bounding box: 9.9 x 6.0 x 1.7 mm
  tessellated surface: 1,608 triangles
  volume: 62 mm^3 (60% of its bounding box)
  symmetry: 2-fold rotationally symmetric about the z axis; mirror-symmetric across its x mid-plane
COMPONENT P176 — geometry summary ("SOIC-20W_7.5x12.8mm_P1.27mm021"; no construction recipe available for this part):
  bounding box: 12.8 x 10.3 x 2.7 mm
  tessellated surface: 1,976 triangles
  volume: 237 mm^3 (65% of its bounding box)
  symmetry: 2-fold rotationally symmetric about the z axis; mirror-symmetric across its x mid-plane, y mid-plane
COMPONENT P177 — geometry summary ("SOIC-14_3.9x8.7mm_P1.27mm007"; no construction recipe available for this part):
  bounding box: 8.7 x 6.0 x 1.8 mm
  tessellated surface: 1,424 triangles
  volume: 54 mm^3 (60% of its bounding box)
  symmetry: 2-fold rotationally symmetric about the z axis; mirror-symmetric across its x mid-plane, y mid-plane
COMPONENT P178 — geometry summary ("SOIC-14_3.9x8.7mm_P1.27mm008"; no construction recipe available for this part):
  bounding box: 8.7 x 6.0 x 1.8 mm
  tessellated surface: 1,424 triangles
  volume: 54 mm^3 (60% of its bounding box)
  symmetry: 2-fold rotationally symmetric about the z axis; mirror-symmetric across its x mid-plane, y mid-plane
COMPONENT P179 — geometry summary ("SOIC-16_3.9x9.9mm_P1.27mm018"; no construction recipe available for this part):
  bounding box: 9.9 x 6.0 x 1.7 mm
  tessellated surface: 1,608 triangles
  volume: 62 mm^3 (60% of its bounding box)
  symmetry: 2-fold rotationally symmetric about the z axis; mirror-symmetric across its x mid-plane
COMPONENT P180 — geometry summary ("SOIC-16_3.9x9.9mm_P1.27mm019"; no construction recipe available for this part):
  bounding box: 9.9 x 6.0 x 1.7 mm
  tessellated surface: 1,608 triangles
  volume: 62 mm^3 (60% of its bounding box)
  symmetry: 2-fold rotationally symmetric about the z axis; mirror-symmetric across its x mid-plane
COMPONENT P181 — geometry summary ("SOIC-16_3.9x9.9mm_P1.27mm020"; no construction recipe available for this part):
  bounding box: 9.9 x 6.0 x 1.7 mm
  tessellated surface: 1,608 triangles
  volume: 62 mm^3 (60% of its bounding box)
  symmetry: 2-fold rotationally symmetric about the z axis; mirror-symmetric across its x mid-plane
COMPONENT P182 — geometry summary ("SOIC-20W_7.5x12.8mm_P1.27mm022"; no construction recipe available for this part):
  bounding box: 12.8 x 10.3 x 2.7 mm
  tessellated surface: 1,976 triangles
  volume: 237 mm^3 (65% of its bounding box)
  symmetry: 2-fold rotationally symmetric about the z axis; mirror-symmetric across its x mid-plane, y mid-plane
COMPONENT P183 — geometry summary ("SOT-23-019"; no construction recipe available for this part):
  bounding box: 2.9 x 2.8 x 1.6 mm
  tessellated surface: 536 triangles
  volume: 7 mm^3 (52% of its bounding box)
  symmetry: mirror-symmetric across its y mid-plane
COMPONENT P184 — geometry summary ("SOIC-20W_7.5x12.8mm_P1.27mm023"; no construction recipe available for this part):
  bounding box: 12.8 x 10.3 x 2.7 mm
  tessellated surface: 1,976 triangles
  volume: 237 mm^3 (65% of its bounding box)
  symmetry: 2-fold rotationally symmetric about the z axis; mirror-symmetric across its x mid-plane, y mid-plane
COMPONENT P185 — geometry summary ("SOIC-20W_7.5x12.8mm_P1.27mm024"; no construction recipe available for this part):
  bounding box: 12.8 x 10.3 x 2.7 mm
  tessellated surface: 1,976 triangles
  volume: 237 mm^3 (65% of its bounding box)
  symmetry: 2-fold rotationally symmetric about the z axis; mirror-symmetric across its x mid-plane, y mid-plane
COMPONENT P186 — geometry summary ("SOIC-20W_7.5x12.8mm_P1.27mm025"; no construction recipe available for this part):
  bounding box: 12.8 x 10.3 x 2.7 mm
  tessellated surface: 1,976 triangles
  volume: 237 mm^3 (65% of its bounding box)
  symmetry: 2-fold rotationally symmetric about the z axis; mirror-symmetric across its x mid-plane, y mid-plane
COMPONENT P187 — geometry summary ("IDC-Header_2x05_P2.54mm_Vertical001"; no construction recipe available for this part):
  bounding box: 20.4 x 12.1 x 9.1 mm
  tessellated surface: 1,320 triangles
  volume: 794 mm^3 (35% of its bounding box)
  symmetry: mirror-symmetric across its x mid-plane
COMPONENT P188 — geometry summary ("C_0805_2012Metric101"; no construction recipe available for this part):
  bounding box: 2.0 x 1.2 x 1.2 mm
  tessellated surface: 188 triangles
  volume: 3 mm^3 (92% of its bounding box)
  symmetry: 4-fold rotationally symmetric about the x axis; 2-fold rotationally symmetric about the z axis; mirror-symmetric across its x mid-plane, y mid-plane
COMPONENT P189 — geometry summary ("C_0805_2012Metric102"; no construction recipe available for this part):
  bounding box: 2.0 x 1.2 x 1.2 mm
  tessellated surface: 188 triangles
  volume: 3 mm^3 (92% of its bounding box)
  symmetry: 4-fold rotationally symmetric about the x axis; 2-fold rotationally symmetric about the z axis; mirror-symmetric across its x mid-plane, y mid-plane
COMPONENT P190 — geometry summary ("C_0805_2012Metric103"; no construction recipe available for this part):
  bounding box: 2.0 x 1.2 x 1.2 mm
  tessellated surface: 188 triangles
  volume: 3 mm^3 (92% of its bounding box)
  symmetry: 4-fold rotationally symmetric about the x axis; 2-fold rotationally symmetric about the z axis; mirror-symmetric across its x mid-plane, y mid-plane
COMPONENT P191 — geometry summary ("C_0805_2012Metric104"; no construction recipe available for this part):
  bounding box: 2.0 x 1.2 x 1.2 mm
  tessellated surface: 188 triangles
  volume: 3 mm^3 (92% of its bounding box)
  symmetry: 4-fold rotationally symmetric about the x axis; 2-fold rotationally symmetric about the z axis; mirror-symmetric across its x mid-plane, y mid-plane
COMPONENT P192 — geometry summary ("C_0805_2012Metric105"; no construction recipe available for this part):
  bounding box: 2.0 x 1.2 x 1.2 mm
  tessellated surface: 188 triangles
  volume: 3 mm^3 (92% of its bounding box)
  symmetry: 4-fold rotationally symmetric about the x axis; 2-fold rotationally symmetric about the z axis; mirror-symmetric across its x mid-plane, y mid-plane
COMPONENT P193 — geometry summary ("C_1206_3216Metric001"; no construction recipe available for this part):
  bounding box: 3.2 x 1.6 x 1.6 mm
  tessellated surface: 188 triangles
  volume: 8 mm^3 (93% of its bounding box)
  symmetry: 2-fold rotationally symmetric about the x axis; 4-fold rotationally symmetric about the y axis; 2-fold rotationally symmetric about the z axis; mirror-symmetric across its z mid-plane
COMPONENT P194 — geometry summary ("C_1206_3216Metric002"; no construction recipe available for this part):
  bounding box: 3.2 x 1.6 x 1.6 mm
  tessellated surface: 188 triangles
  volume: 8 mm^3 (93% of its bounding box)
  symmetry: 2-fold rotationally symmetric about the x axis; 4-fold rotationally symmetric about the y axis; 2-fold rotationally symmetric about the z axis; mirror-symmetric across its z mid-plane
COMPONENT P195 — geometry summary ("C_1206_3216Metric003"; no construction recipe available for this part):
  bounding box: 3.2 x 1.6 x 1.6 mm
  tessellated surface: 188 triangles
  volume: 8 mm^3 (93% of its bounding box)
  symmetry: 2-fold rotationally symmetric about the x axis; 4-fold rotationally symmetric about the y axis; 2-fold rotationally symmetric about the z axis; mirror-symmetric across its z mid-plane
COMPONENT P196 — geometry summary ("C_1206_3216Metric004"; no construction recipe available for this part):
  bounding box: 3.2 x 1.6 x 1.6 mm
  tessellated surface: 188 triangles
  volume: 8 mm^3 (93% of its bounding box)
  symmetry: 2-fold rotationally symmetric about the x axis; 4-fold rotationally symmetric about the y axis; 2-fold rotationally symmetric about the z axis; mirror-symmetric across its z mid-plane
COMPONENT P197 — geometry summary ("C_1206_3216Metric005"; no construction recipe available for this part):
  bounding box: 3.2 x 1.6 x 1.6 mm
  tessellated surface: 188 triangles
  volume: 8 mm^3 (93% of its bounding box)
  symmetry: 2-fold rotationally symmetric about the x axis; 4-fold rotationally symmetric about the y axis; 2-fold rotationally symmetric about the z axis; mirror-symmetric across its z mid-plane
COMPONENT P198 — geometry summary ("C_1206_3216Metric006"; no construction recipe available for this part):
  bounding box: 3.2 x 1.6 x 1.6 mm
  tessellated surface: 188 triangles
  volume: 8 mm^3 (93% of its bounding box)
  symmetry: 2-fold rotationally symmetric about the x axis; 4-fold rotationally symmetric about the y axis; 2-fold rotationally symmetric about the z axis; mirror-symmetric across its z mid-plane
COMPONENT P199 — geometry summary ("C_1206_3216Metric007"; no construction recipe available for this part):
  bounding box: 3.2 x 1.6 x 1.6 mm
  tessellated surface: 188 triangles
  volume: 8 mm^3 (93% of its bounding box)
  symmetry: 2-fold rotationally symmetric about the x axis; 4-fold rotationally symmetric about the y axis; 2-fold rotationally symmetric about the z axis; mirror-symmetric across its z mid-plane
COMPONENT P200 — geometry summary ("C_1206_3216Metric008"; no construction recipe available for this part):
  bounding box: 3.2 x 1.6 x 1.6 mm
  tessellated surface: 188 triangles
  volume: 8 mm^3 (93% of its bounding box)
  symmetry: 2-fold rotationally symmetric about the x axis; 4-fold rotationally symmetric about the y axis; 2-fold rotationally symmetric about the z axis; mirror-symmetric across its z mid-plane
COMPONENT P201 — geometry summary ("C_1206_3216Metric009"; no construction recipe available for this part):
  bounding box: 3.2 x 1.6 x 1.6 mm
  tessellated surface: 188 triangles
  volume: 8 mm^3 (93% of its bounding box)
  symmetry: 2-fold rotationally symmetric about the x axis; 4-fold rotationally symmetric about the y axis; 2-fold rotationally symmetric about the z axis; mirror-symmetric across its z mid-plane
COMPONENT P202 — geometry summary ("C_1206_3216Metric010"; no construction recipe available for this part):
  bounding box: 3.2 x 1.6 x 1.6 mm
  tessellated surface: 188 triangles
  volume: 8 mm^3 (93% of its bounding box)
  symmetry: 2-fold rotationally symmetric about the x axis; 4-fold rotationally symmetric about the y axis; 2-fold rotationally symmetric about the z axis; mirror-symmetric across its z mid-plane
COMPONENT P203 — geometry summary ("C_1206_3216Metric011"; no construction recipe available for this part):
  bounding box: 3.2 x 1.6 x 1.6 mm
  tessellated surface: 188 triangles
  volume: 8 mm^3 (93% of its bounding box)
  symmetry: 2-fold rotationally symmetric about the x axis; 4-fold rotationally symmetric about the y axis; 2-fold rotationally symmetric about the z axis; mirror-symmetric across its z mid-plane
COMPONENT P204 — geometry summary ("C_1206_3216Metric012"; no construction recipe available for this part):
  bounding box: 3.2 x 1.6 x 1.6 mm
  tessellated surface: 188 triangles
  volume: 8 mm^3 (93% of its bounding box)
  symmetry: 2-fold rotationally symmetric about the x axis; 4-fold rotationally symmetric about the y axis; 2-fold rotationally symmetric about the z axis; mirror-symmetric across its z mid-plane
COMPONENT P205 — geometry summary ("D_SMC001"; no construction recipe available for this part):
  bounding box: 8.0 x 5.9 x 2.3 mm
  tessellated surface: 164 triangles
  volume: 100 mm^3 (92% of its bounding box)
  symmetry: mirror-symmetric across its x mid-plane, y mid-plane
COMPONENT P206 — geometry summary ("R_0805_2012Metric014"; no construction recipe available for this part):
  bounding box: 2.0 x 1.2 x 0.4 mm
  tessellated surface: 148 triangles
  volume: 1 mm^3 (93% of its bounding box)
  symmetry: mirror-symmetric across its x mid-plane, y mid-plane
COMPONENT P207 — geometry summary ("R_0805_2012Metric015"; no construction recipe available for this part):
  bounding box: 2.0 x 1.2 x 0.4 mm
  tessellated surface: 148 triangles
  volume: 1 mm^3 (93% of its bounding box)
  symmetry: mirror-symmetric across its x mid-plane, y mid-plane
COMPONENT P208 — geometry summary ("R_0805_2012Metric016"; no construction recipe available for this part):
  bounding box: 2.0 x 1.2 x 0.4 mm
  tessellated surface: 148 triangles
  volume: 1 mm^3 (93% of its bounding box)
  symmetry: mirror-symmetric across its x mid-plane, y mid-plane
COMPONENT P209 — geometry summary ("R_0805_2012Metric017"; no construction recipe available for this part):
  bounding box: 2.0 x 1.2 x 0.4 mm
  tessellated surface: 148 triangles
  volume: 1 mm^3 (93% of its bounding box)
  symmetry: mirror-symmetric across its x mid-plane, y mid-plane
COMPONENT P210 — geometry summary ("R_0805_2012Metric018"; no construction recipe available for this part):
  bounding box: 2.0 x 1.2 x 0.4 mm
  tessellated surface: 148 triangles
  volume: 1 mm^3 (93% of its bounding box)
  symmetry: mirror-symmetric across its x mid-plane, y mid-plane
COMPONENT P211 — geometry summary ("SOT-23-020"; no construction recipe available for this part):
  bounding box: 2.9 x 2.8 x 1.6 mm
  tessellated surface: 628 triangles
  volume: 7 mm^3 (52% of its bounding box)
  symmetry: 2-fold rotationally symmetric about the z axis; mirror-symmetric across its x mid-plane, y mid-plane
COMPONENT P212 — geometry summary ("FirstPartPeripheralsTop"; no construction recipe available for this part):
  bounding box: 145.0 x 132.5 x 58.0 mm
  tessellated surface: 596 triangles
  volume: 114848 mm^3 (10% of its bounding box)
COMPONENT P213 — geometry summary ("SecondPartPeripheralsTop"; no construction recipe available for this part):
  bounding box: 131.0 x 78.0 x 58.0 mm
  tessellated surface: 498 triangles
  volume: 56774 mm^3 (10% of its bounding box)
COMPONENT P214 — geometry summary ("SecondPartProcessorTop"; no construction recipe available for this part):
  bounding box: 120.6 x 78.0 x 58.0 mm
  tessellated surface: 2,650 triangles
  volume: 49472 mm^3 (9% of its bounding box)
COMPONENT P215 — geometry summary ("FirstPartProcessorTop"; no construction recipe available for this part):
  bounding box: 147.0 x 120.6 x 58.0 mm
  tessellated surface: 16,622 triangles
  volume: 108127 mm^3 (11% of its bounding box)
PROVENANCE & LICENSES
A FreeCAD (.FCStd) document from a public repository crawl; recipes are the document's own serialized feature recipes (and, for linked parts, companion documents' recipes).
License: cc-by-4.0.
